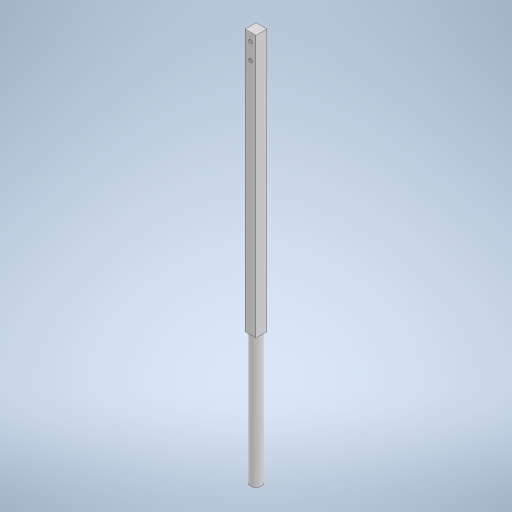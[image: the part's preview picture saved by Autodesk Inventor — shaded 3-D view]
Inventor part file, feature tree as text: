
AUTODESK INVENTOR PART (.ipt)
format: ipt  version: 2023 (Build 270158000, 158)  size: 266,240 bytes
history: native  units: in
note: dims shown in document units (in); Inventor stores cm internally (conversion verified against a paired STEP export)
features: sketch x3, extrude x2, hole x1
ambient origin geometry x8: Origin, YZ Plane, XZ Plane, XY Plane, X Axis, Y Axis, Z Axis, Center Point
bodies: Solid1 (feature_tree)
feature tree (6):
  extrude  "Extrusion1"  Depth=0.25in
  extrude  "Extrusion3"  Depth=0.25in
  hole  "Hole1"  [1 undecoded]
  sketch  "Sketch1"  dims[d0=0.25in d1=0.25in]
  sketch  "Sketch3"  dims[d2=6.0in d3=0.0in d12=0.25in]
  sketch  "Sketch4"  dims[d13=3.0in d14=0.0in d15=0.1875in d16=0.112in d17=0.375in d18=0.112in d25=0.0849in d26=0.75in d27=0.375in d28=0.25in d29=0.5635in d30=1.0in d31=0.8108in d11=0.0in]
note: 1 required parameter value undecoded (feature->parameter linkage not recoverable at this tier; creation-order binding heuristic only, values carry confidence <= 0.55)
